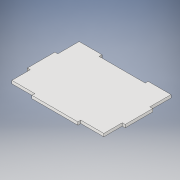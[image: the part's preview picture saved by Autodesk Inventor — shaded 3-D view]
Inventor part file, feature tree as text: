
AUTODESK INVENTOR PART (.ipt)
format: ipt  version: 2019 (Build 230136000, 136)  size: 132,608 bytes
history: native  units: mm
features: other x1, extrude x1, sketch x1
ambient origin geometry x8: Origin, YZ Plane, XZ Plane, XY Plane, X Axis, Y Axis, Z Axis, Center Point
bodies: Body1 (feature_tree)
feature tree (3):
  other  "Sólido1"
  extrude  "Extrusión1"  Depth=3.18mm
  sketch  "Boceto1"  dims[d0=100.0mm d1=73.18mm d2=3.18mm d3=50.0mm d4=25.0mm d6=30.0mm d8=20.0mm d10=50.0mm d11=25.0mm d16=3.18mm d17=20.0mm d18=30.0mm d19=3.18mm d20=0.0mm]
